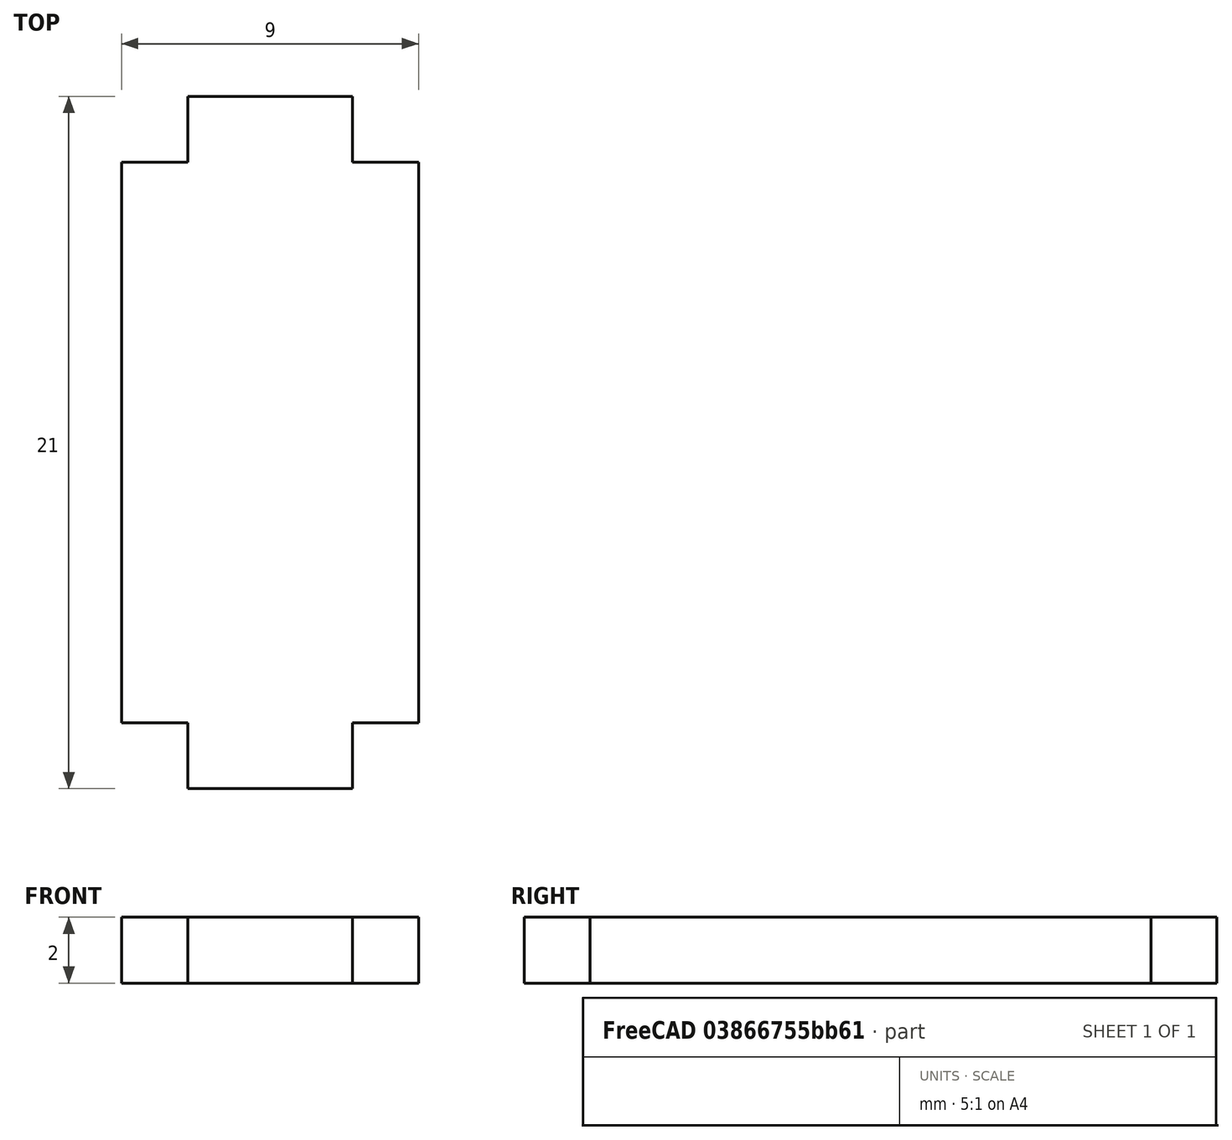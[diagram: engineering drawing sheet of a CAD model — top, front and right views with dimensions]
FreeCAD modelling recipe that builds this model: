
FCSTD DOCUMENT  (FreeCAD 0.18R16131 (Git))
Label: tibia_poutre
License: All rights reserved
LicenseURL: http://en.wikipedia.org/wiki/All_rights_reserved
objects: Sketcher::SketchObject×1, PartDesign::Pad×1, PartDesign::Body×1
note: 4 computed .brp shape members not serialized (recipe doc carries the construction recipe); baked Part::Feature solids carry a one-line shape summary decoded from their .brp

FEATURE [Sketcher::SketchObject] Sketch
  MapMode = 5
  Support = -> [XY_Plane]
  sketch-geometry (12):
    g0: LineSegment StartX=0 StartY=19 StartZ=0 EndX=2 EndY=19 EndZ=0
    g1: LineSegment StartX=2 StartY=19 StartZ=0 EndX=2 EndY=21 EndZ=0
    g2: LineSegment StartX=2 StartY=21 StartZ=0 EndX=7 EndY=21 EndZ=0
    g3: LineSegment StartX=7 StartY=21 StartZ=0 EndX=7 EndY=19 EndZ=0
    g4: LineSegment StartX=7 StartY=19 StartZ=0 EndX=9 EndY=19 EndZ=0
    g5: LineSegment StartX=9 StartY=19 StartZ=0 EndX=9 EndY=2 EndZ=0
    g6: LineSegment StartX=9 StartY=2 StartZ=0 EndX=7 EndY=2 EndZ=0
    g7: LineSegment StartX=7 StartY=2 StartZ=0 EndX=7 EndY=0 EndZ=0
    g8: LineSegment StartX=7 StartY=0 StartZ=0 EndX=2 EndY=0 EndZ=0
    g9: LineSegment StartX=2 StartY=0 StartZ=0 EndX=2 EndY=2 EndZ=0
    g10: LineSegment StartX=2 StartY=2 StartZ=0 EndX=0 EndY=2 EndZ=0
    g11: LineSegment StartX=0 StartY=2 StartZ=0 EndX=0 EndY=19 EndZ=0
  constraints (36):
    c: Coincident(g0,g1)
    c: Coincident(g1,g2)
    c: Coincident(g2,g3)
    c: Coincident(g3,g4)
    c: Coincident(g4,g5)
    c: Coincident(g5,g6)
    c: Coincident(g6,g7)
    c: Coincident(g7,g8)
    c: Coincident(g8,g9)
    c: Coincident(g9,g10)
    c: Coincident(g10,g11)
    c: Coincident(g11,g0)
    c: Vertical(g11)
    c: Vertical(g1)
    c: Vertical(g3)
    c: Vertical(g5)
    c: Vertical(g7)
    c: Vertical(g9)
    c: PointOnObject(g10,g-2)
    c: PointOnObject(g8,g-1)
    c: Horizontal(g8)
    c: Horizontal(g2)
    c: Horizontal(g0)
    c: Horizontal(g4)
    c: Horizontal(g6)
    c: Horizontal(g10)
    c: Horizontal(g0,g3)
    c: Horizontal(g6,g9)
    c: Vertical(g0,g9)
    c: Vertical(g3,g6)
    c: DistanceX(g0,g4) = 9
    c: DistanceX(g2,g2) = 5
    c: DistanceY(g1,g1) = 2
    c: DistanceX(g0,g0) = 2
    c: DistanceY(g11,g11) = 17
    c: Equal(g1,g9)
FEATURE [PartDesign::Pad] Pad
  Length = 2
  Length2 = 100
  Profile = -> Sketch
  Type = 0
FEATURE [PartDesign::Body] Body
  Group = -> [Sketch,Pad]
  Origin = -> Origin
  Tip = -> Pad
